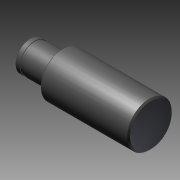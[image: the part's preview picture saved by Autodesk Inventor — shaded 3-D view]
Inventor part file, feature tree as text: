
AUTODESK INVENTOR PART (.ipt)
format: ipt  version: 2011 SP1 (Build 150282100, 282)  size: 113,152 bytes
history: native  units: mm
features: revolve x2, sketch x2
ambient origin geometry x8: Origin, YZ Plane, XZ Plane, XY Plane, X Axis, Y Axis, Z Axis, Center Point
bodies: Solid1 (feature_tree)
feature tree (4):
  revolve  "Revolution1"  Angle=360.0deg
  revolve  "Revolution2"  [1 undecoded]
  sketch  "Sketch_1"  dims[d0=360.0deg d1=360.0deg]
  sketch  "Sketch_40"
note: 1 required parameter value undecoded (feature->parameter linkage not recoverable at this tier; creation-order binding heuristic only, values carry confidence <= 0.55)
